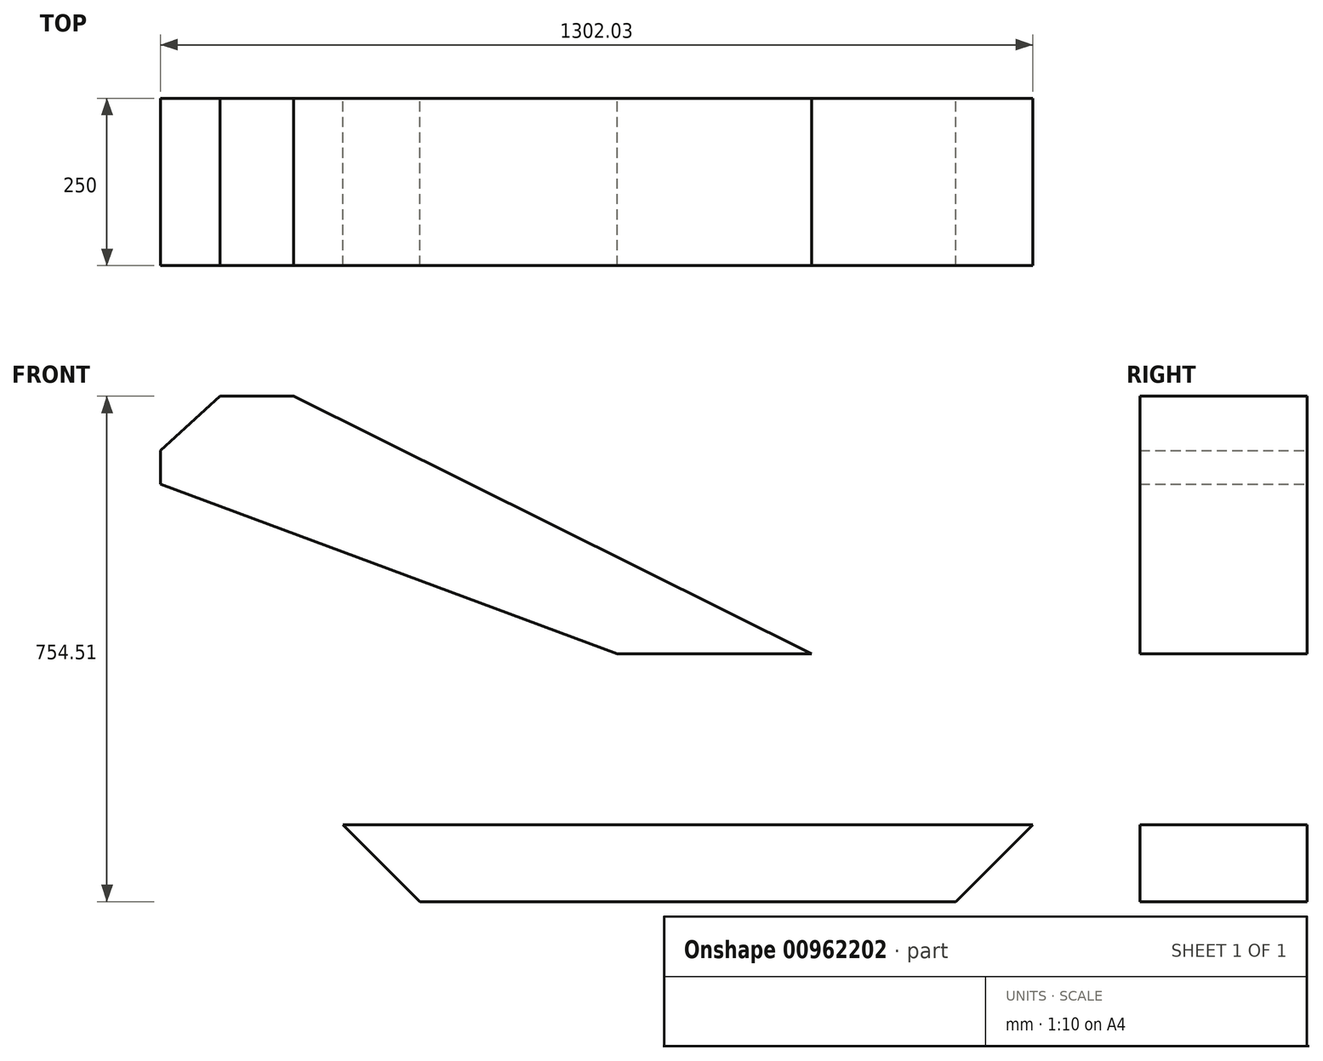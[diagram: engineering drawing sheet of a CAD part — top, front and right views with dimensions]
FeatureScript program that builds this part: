
annotation { "Feature Type Name" : "Feature", "Feature Type Description" : "" }
export const myFeature = defineFeature(function(context is Context, id is Id, definition is map)
    precondition{}
    {
        {
            var Q0;
            Q0=qCreatedBy(makeId("Front.planeOp"),FACE);
            var sketch = newSketch(context, id + "F0", { "sketchPlane" : qUnion([Q0])});
            skLineSegment(sketch, "E0", {"start": v(0, 0) * mm, "end": v(1030, 0) * mm});
            skLineSegment(sketch, "E1", {"start": v(1030, 0) * mm, "end": v(915, -115) * mm});
            skLineSegment(sketch, "E2", {"start": v(915, -115) * mm, "end": v(115, -115) * mm});
            skLineSegment(sketch, "E3", {"start": v(0, 0) * mm, "end": v(115, -115) * mm});
            skLineSegment(sketch, "E4", {"start": v(410, 255) * mm, "end": v(700, 255) * mm});
            skLineSegment(sketch, "E5", {"start": v(700, 255) * mm, "end": v(-73.42, 639.5) * mm});
            skLineSegment(sketch, "E6", {"start": v(-73.42, 639.5) * mm, "end": v(-183.42, 639.5) * mm});
            skLineSegment(sketch, "E7", {"start": v(-183.42, 639.5) * mm, "end": v(-272.03, 558.6) * mm});
            skLineSegment(sketch, "E8", {"start": v(-272.03, 558.6) * mm, "end": v(-272.03, 508.6) * mm});
            skLineSegment(sketch, "E9", {"start": v(-272.03, 508.6) * mm, "end": v(410, 255) * mm});
            skLineSegment(sketch, "E10", {"start": v(336.77, 639.5) * mm, "end": v(-626.34, 639.5) * mm, "construction": true});
            skSolve(sketch);
        }
        {
            var Q0;
            Q0=qSketchRegion(id+"F0",true);
            extrude(context, id + "F1", {"entities" : qUnion([Q0]), "depth" : 250 * mm, "offsetDistance" : 25 * mm});
        }
    });
